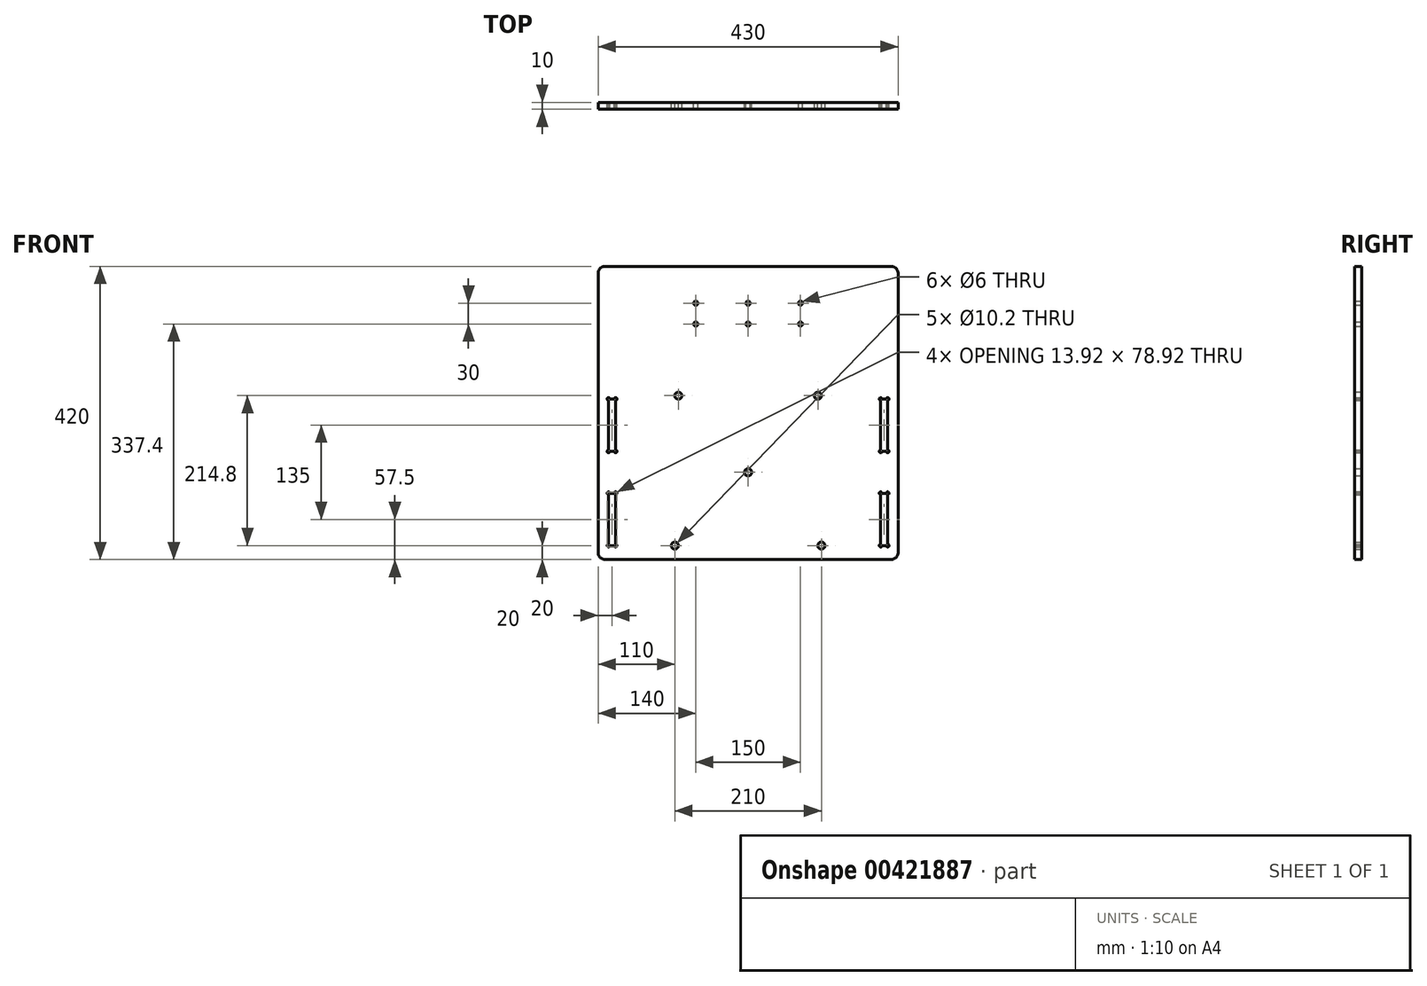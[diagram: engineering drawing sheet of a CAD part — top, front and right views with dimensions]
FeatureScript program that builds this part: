
annotation { "Feature Type Name" : "Feature", "Feature Type Description" : "" }
export const myFeature = defineFeature(function(context is Context, id is Id, definition is map)
    precondition{}
    {
        {
            var Q0;
            Q0=qCreatedBy(makeId("Front.planeOp"),FACE);
            var sketch = newSketch(context, id + "F0", { "sketchPlane" : qUnion([Q0])});
            skLineSegment(sketch, "E0", {"start": v(0, -71.17) * mm, "end": v(0, 456.65) * mm, "construction": true});
            skLineSegment(sketch, "E1", {"start": v(0, 0) * mm, "end": v(-215, 0) * mm});
            skLineSegment(sketch, "E2", {"start": v(-215, 0) * mm, "end": v(-215, 420) * mm});
            skLineSegment(sketch, "E3", {"start": v(-215, 420) * mm, "end": v(0, 420) * mm});
            skCircle(sketch, "E4", {"center": v(-105, 20) * mm, "radius": 5.1 * mm});
            skCircle(sketch, "E5", {"center": v(-100, 234.8) * mm, "radius": 5.1 * mm});
            skArc(sketch, "E6", {"start": v(0, 130.1) * mm, "mid": v(-5.1, 125) * mm, "end": v(0, 119.9) * mm});
            skArc(sketch, "E7", {"start": v(0, 370.4) * mm, "mid": v(-3, 367.4) * mm, "end": v(0, 364.4) * mm});
            skLineSegment(sketch, "E8", {"start": v(0, 367.4) * mm, "end": v(-84.52, 367.4) * mm, "construction": true});
            skCircle(sketch, "E9", {"center": v(-75, 367.4) * mm, "radius": 3 * mm});
            skLineSegment(sketch, "E10", {"start": v(0, 352.4) * mm, "end": v(-81.22, 352.4) * mm, "construction": true});
            skCircle(sketch, "E11.MirrorC", {"center": v(-75, 337.4) * mm, "radius": 3 * mm});
            skArc(sketch, "E12.MirrorCS", {"start": v(0, 334.4) * mm, "mid": v(-3, 337.4) * mm, "end": v(0, 340.4) * mm});
            skLineSegment(sketch, "E13", {"start": v(-200, 22) * mm, "end": v(-200, 93) * mm});
            skLineSegment(sketch, "E14", {"start": v(-190, 22) * mm, "end": v(-190, 93) * mm});
            skLineSegment(sketch, "E15", {"start": v(-198, 20) * mm, "end": v(-192, 20) * mm});
            skPoint(sketch, "E16.orphan", {"position": v(-200, 0) * mm});
            skLineSegment(sketch, "E17", {"start": v(-198, 95) * mm, "end": v(-192, 95) * mm});
            skLineSegment(sketch, "E18", {"start": v(-200, 155) * mm, "end": v(-190, 155) * mm});
            skLineSegment(sketch, "E19.trimOffspring", {"start": v(-200, 155) * mm, "end": v(-200, 228) * mm});
            skLineSegment(sketch, "E20.trimOffspring", {"start": v(-190, 155) * mm, "end": v(-190, 228) * mm});
            skLineSegment(sketch, "E21", {"start": v(-198, 230) * mm, "end": v(-192, 230) * mm});
            skArc(sketch, "E22", {"start": v(-192, 20) * mm, "mid": v(-188.59, 18.59) * mm, "end": v(-190, 22) * mm});
            skArc(sketch, "E23", {"start": v(-200, 22) * mm, "mid": v(-201.41, 18.59) * mm, "end": v(-198, 20) * mm});
            skArc(sketch, "E24", {"start": v(-200, 93) * mm, "mid": v(-201.41, 96.41) * mm, "end": v(-198, 95) * mm});
            skArc(sketch, "E25", {"start": v(-192, 95) * mm, "mid": v(-188.59, 96.41) * mm, "end": v(-190, 93) * mm});
            skArc(sketch, "E26", {"start": v(-200, 157) * mm, "mid": v(-201.41, 153.59) * mm, "end": v(-198, 155) * mm});
            skArc(sketch, "E27", {"start": v(-192, 155) * mm, "mid": v(-188.59, 153.59) * mm, "end": v(-190, 157) * mm});
            skArc(sketch, "E28", {"start": v(-200, 228) * mm, "mid": v(-201.41, 231.41) * mm, "end": v(-198, 230) * mm});
            skArc(sketch, "E29", {"start": v(-192, 230) * mm, "mid": v(-188.59, 231.41) * mm, "end": v(-190, 228) * mm});
            skArc(sketch, "E30.MirrorCS", {"start": v(192, 155) * mm, "mid": v(188.59, 153.59) * mm, "end": v(190, 157) * mm});
            skArc(sketch, "E31.MirrorCS", {"start": v(192, 95) * mm, "mid": v(188.59, 96.41) * mm, "end": v(190, 93) * mm});
            skArc(sketch, "E32.MirrorCS", {"start": v(192, 20) * mm, "mid": v(188.59, 18.59) * mm, "end": v(190, 22) * mm});
            skLineSegment(sketch, "E33.MirrorCS", {"start": v(200, 155) * mm, "end": v(190, 155) * mm});
            skLineSegment(sketch, "E34.MirrorCS", {"start": v(198, 20) * mm, "end": v(192, 20) * mm});
            skArc(sketch, "E35.MirrorCS", {"start": v(200, 157) * mm, "mid": v(201.41, 153.59) * mm, "end": v(198, 155) * mm});
            skLineSegment(sketch, "E36.MirrorCS", {"start": v(198, 95) * mm, "end": v(192, 95) * mm});
            skArc(sketch, "E37.MirrorCS", {"start": v(200, 22) * mm, "mid": v(201.41, 18.59) * mm, "end": v(198, 20) * mm});
            skLineSegment(sketch, "E38.MirrorCS", {"start": v(198, 230) * mm, "end": v(192, 230) * mm});
            skArc(sketch, "E39.MirrorCS", {"start": v(200, 93) * mm, "mid": v(201.41, 96.41) * mm, "end": v(198, 95) * mm});
            skArc(sketch, "E40.MirrorCS", {"start": v(192, 230) * mm, "mid": v(188.59, 231.41) * mm, "end": v(190, 228) * mm});
            skArc(sketch, "E41.MirrorCS", {"start": v(200, 228) * mm, "mid": v(201.41, 231.41) * mm, "end": v(198, 230) * mm});
            skArc(sketch, "E42.MirrorCS", {"start": v(0, 370.4) * mm, "mid": v(3, 367.4) * mm, "end": v(0, 364.4) * mm});
            skArc(sketch, "E43.MirrorCS", {"start": v(0, 130.1) * mm, "mid": v(5.1, 125) * mm, "end": v(0, 119.9) * mm});
            skArc(sketch, "E44.MirrorCS", {"start": v(0, 334.4) * mm, "mid": v(3, 337.4) * mm, "end": v(0, 340.4) * mm});
            skCircle(sketch, "E45.MirrorC", {"center": v(75, 367.4) * mm, "radius": 3 * mm});
            skCircle(sketch, "E46.MirrorC", {"center": v(100, 234.8) * mm, "radius": 5.1 * mm});
            skCircle(sketch, "E47.MirrorC", {"center": v(105, 20) * mm, "radius": 5.1 * mm});
            skCircle(sketch, "E48.MirrorC", {"center": v(75, 337.4) * mm, "radius": 3 * mm});
            skLineSegment(sketch, "E49.MirrorCS", {"start": v(190, 155) * mm, "end": v(190, 228) * mm});
            skLineSegment(sketch, "E50.MirrorCS", {"start": v(200, 22) * mm, "end": v(200, 93) * mm});
            skLineSegment(sketch, "E51.MirrorCS", {"start": v(190, 22) * mm, "end": v(190, 93) * mm});
            skLineSegment(sketch, "E52.MirrorCS", {"start": v(0, 0) * mm, "end": v(215, 0) * mm});
            skLineSegment(sketch, "E53.MirrorCS", {"start": v(215, 420) * mm, "end": v(0, 420) * mm});
            skLineSegment(sketch, "E54.MirrorCS", {"start": v(215, 0) * mm, "end": v(215, 420) * mm});
            skLineSegment(sketch, "E55.MirrorCS", {"start": v(200, 155) * mm, "end": v(200, 228) * mm});
            skPoint(sketch, "E56.MirrorP", {"position": v(200, 0) * mm});
            skLineSegment(sketch, "E57.MirrorCS", {"start": v(0, 367.4) * mm, "end": v(84.52, 367.4) * mm, "construction": true});
            skLineSegment(sketch, "E58.MirrorCS", {"start": v(0, 352.4) * mm, "end": v(81.22, 352.4) * mm, "construction": true});
            skSolve(sketch);
        }
        {
            var Q0;
            Q0=makeQuery(id+"F0.imprint","IMPRINT",FACE,{"disambiguationData":[TD([[makeQuery(id+"F0.imprint","IMPRINT",EDGE,{"derivedFrom":sQuery(id+"F0.wireOp",EDGE,"E1")}),-1.0]])]});
            extrude(context, id + "F1", {"entities" : qUnion([Q0]), "depth" : 10 * mm});
        }
        {
            var Q0;
            Q0=makeQuery(id+"F1.opExtrude","SWEPT_EDGE",EDGE,{"disambiguationData":[OSD([sQuery(id+"F0.wireOp",EDGE,"E52.MirrorCS"),sQuery(id+"F0.wireOp",EDGE,"E54.MirrorCS")])]});
            var Q1;
            Q1=makeQuery(id+"F1.opExtrude","SWEPT_EDGE",EDGE,{"disambiguationData":[OSD([sQuery(id+"F0.wireOp",EDGE,"E53.MirrorCS"),sQuery(id+"F0.wireOp",EDGE,"E54.MirrorCS")])]});
            var Q2;
            Q2=makeQuery(id+"F1.opExtrude","SWEPT_EDGE",EDGE,{"disambiguationData":[OSD([sQuery(id+"F0.wireOp",EDGE,"E2"),sQuery(id+"F0.wireOp",EDGE,"E3")])]});
            var Q3;
            Q3=makeQuery(id+"F1.opExtrude","SWEPT_EDGE",EDGE,{"disambiguationData":[OSD([sQuery(id+"F0.wireOp",EDGE,"E1"),sQuery(id+"F0.wireOp",EDGE,"E2")])]});
            fillet(context, id + "F2", {"entities" : qUnion([Q0, Q1, Q2, Q3]), "radius" : 10 * mm, "tangentPropagation" : true, "allowEdgeOverflow" : false});
        }
    });
